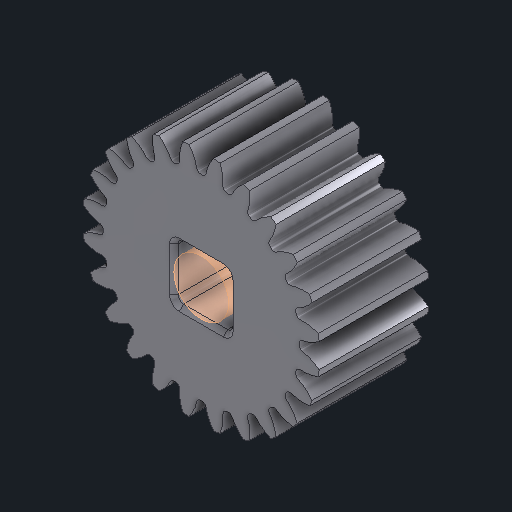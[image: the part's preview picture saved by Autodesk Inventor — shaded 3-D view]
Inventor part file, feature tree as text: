
AUTODESK INVENTOR PART (.ipt)
format: ipt  version: 2025 (Build 290162000, 162)  size: 466,432 bytes
history: native  units: in
note: dims shown in document units (in); Inventor stores cm internally (conversion verified against a paired STEP export)
features: other x5, sketch x1
ambient origin geometry x8: Origin, YZ Plane, XZ Plane, XY Plane, X Axis, Y Axis, Z Axis, Center Point
bodies: Solid1 (feature_tree)
feature tree (6):
  other  "HS 24T Gear, No Insert.ipt"
  other  "Solid1::HS 24T Gear, No Insert.ipt"
  other  "TaggingFeature1"
  sketch  "Sketch1"  dims[d0=0.3937in]
  other  "Srf1"
  other  "Srf1::Derived"
